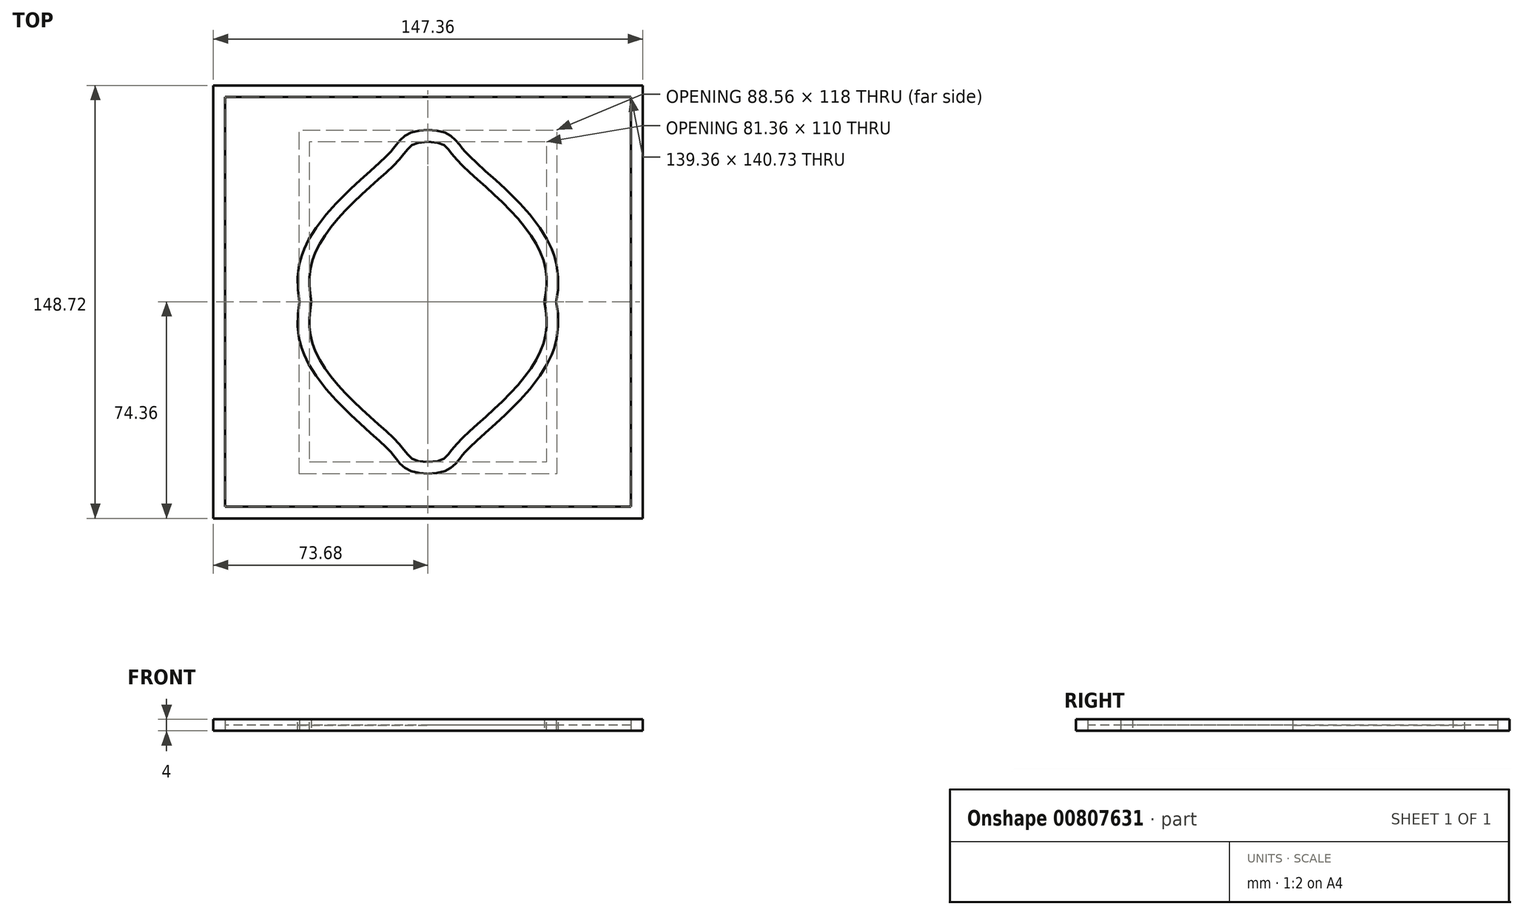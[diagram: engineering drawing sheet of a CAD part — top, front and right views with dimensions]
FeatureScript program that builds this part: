
annotation { "Feature Type Name" : "Feature", "Feature Type Description" : "" }
export const myFeature = defineFeature(function(context is Context, id is Id, definition is map)
    precondition{}
    {
        {
            var Q0;
            Q0=qCreatedBy(makeId("Top.planeOp"),FACE);
            var sketch = newSketch(context, id + "F0", { "sketchPlane" : qUnion([Q0])});
            skFitSpline(sketch, "E0", {"points": [v(-40, 0) * mm, v(-39.3, 15.26) * mm, v(-25.49, 34.27) * mm, v(-8.78, 50.1) * mm, v(0, 55) * mm], "startDerivative": vector(-12.5, 67.43) * mm, "endDerivative": vector(94.36, 0) * mm});
            skFitSpline(sketch, "E1.MirrorCS", {"points": [v(40, 0) * mm, v(39.3, 15.26) * mm, v(25.49, 34.27) * mm, v(8.78, 50.1) * mm, v(0, 55) * mm], "startDerivative": vector(12.5, 67.43) * mm, "endDerivative": vector(-94.36, 0) * mm});
            skFitSpline(sketch, "E2.MirrorCS", {"points": [v(-40, 0) * mm, v(-39.3, -15.26) * mm, v(-25.49, -34.27) * mm, v(-8.78, -50.1) * mm, v(0, -55) * mm], "startDerivative": vector(-12.5, -67.43) * mm, "endDerivative": vector(94.36, 0) * mm});
            skFitSpline(sketch, "E3.MirrorCS", {"points": [v(40, 0) * mm, v(39.3, -15.26) * mm, v(25.49, -34.27) * mm, v(8.78, -50.1) * mm, v(0, -55) * mm], "startDerivative": vector(12.5, -67.43) * mm, "endDerivative": vector(-94.36, 0) * mm});
            skFitSpline(sketch, "E4.0", {"points": [v(43.93, -0.73) * mm, v(44.07, 0.02) * mm, v(44.32, 1.53) * mm, v(44.59, 3.8) * mm, v(44.73, 6.09) * mm, v(44.7, 8.4) * mm, v(44.51, 10.74) * mm, v(44.18, 12.7) * mm, v(43.8, 14.28) * mm, v(43.52, 15.27) * mm, v(43.26, 16.07) * mm, v(43.06, 16.66) * mm, v(42.83, 17.25) * mm, v(42.52, 18.04) * mm, v(42.1, 19.02) * mm, v(41.35, 20.57) * mm, v(40.3, 22.49) * mm, v(38.89, 24.75) * mm, v(36.79, 27.73) * mm, v(34.43, 30.64) * mm, v(32.18, 33.13) * mm, v(30.86, 34.53) * mm, v(29.84, 35.58) * mm, v(28.81, 36.6) * mm, v(27.76, 37.63) * mm, v(26.7, 38.64) * mm, v(25.29, 39.97) * mm, v(23.52, 41.6) * mm, v(21.42, 43.47) * mm, v(19.4, 45.27) * mm, v(17.8, 46.7) * mm, v(16.6, 47.8) * mm, v(15.74, 48.6) * mm, v(14.94, 49.37) * mm, v(14.18, 50.11) * mm, v(13.6, 50.7) * mm, v(13.17, 51.16) * mm, v(12.86, 51.48) * mm, v(12.58, 51.8) * mm, v(12.35, 52.06) * mm, v(12.18, 52.26) * mm, v(12.06, 52.4) * mm, v(11.94, 52.54) * mm, v(11.83, 52.68) * mm, v(11.72, 52.82) * mm, v(11.57, 53.01) * mm, v(11.39, 53.26) * mm, v(11.16, 53.56) * mm, v(10.92, 53.88) * mm, v(10.67, 54.21) * mm, v(10.4, 54.56) * mm, v(10.1, 54.93) * mm, v(9.79, 55.3) * mm, v(9.43, 55.68) * mm, v(9.04, 56.07) * mm, v(8.6, 56.46) * mm, v(8.14, 56.83) * mm, v(7.62, 57.19) * mm, v(7.07, 57.52) * mm, v(6.48, 57.82) * mm, v(5.86, 58.09) * mm, v(5.22, 58.32) * mm, v(4.33, 58.57) * mm, v(3.16, 58.8) * mm, v(1.66, 58.97) * mm, v(0.57, 59) * mm, v(0, 59) * mm]});
            skFitSpline(sketch, "E4.1", {"points": [v(43.93, 0.73) * mm, v(44.07, -0.02) * mm, v(44.32, -1.53) * mm, v(44.59, -3.8) * mm, v(44.73, -6.09) * mm, v(44.7, -8.4) * mm, v(44.51, -10.74) * mm, v(44.18, -12.7) * mm, v(43.8, -14.28) * mm, v(43.52, -15.27) * mm, v(43.26, -16.07) * mm, v(43.06, -16.66) * mm, v(42.83, -17.25) * mm, v(42.52, -18.04) * mm, v(42.1, -19.02) * mm, v(41.35, -20.57) * mm, v(40.3, -22.49) * mm, v(38.89, -24.75) * mm, v(36.79, -27.73) * mm, v(34.43, -30.64) * mm, v(32.18, -33.13) * mm, v(30.86, -34.53) * mm, v(29.84, -35.58) * mm, v(28.81, -36.6) * mm, v(27.76, -37.63) * mm, v(26.7, -38.64) * mm, v(25.29, -39.97) * mm, v(23.52, -41.6) * mm, v(21.42, -43.47) * mm, v(19.4, -45.27) * mm, v(17.8, -46.7) * mm, v(16.6, -47.8) * mm, v(15.74, -48.6) * mm, v(14.94, -49.37) * mm, v(14.18, -50.11) * mm, v(13.6, -50.7) * mm, v(13.17, -51.16) * mm, v(12.86, -51.48) * mm, v(12.58, -51.8) * mm, v(12.35, -52.06) * mm, v(12.18, -52.26) * mm, v(12.06, -52.4) * mm, v(11.94, -52.54) * mm, v(11.83, -52.68) * mm, v(11.72, -52.82) * mm, v(11.57, -53.01) * mm, v(11.39, -53.26) * mm, v(11.16, -53.56) * mm, v(10.92, -53.88) * mm, v(10.67, -54.21) * mm, v(10.4, -54.56) * mm, v(10.1, -54.93) * mm, v(9.79, -55.3) * mm, v(9.43, -55.68) * mm, v(9.04, -56.07) * mm, v(8.6, -56.46) * mm, v(8.14, -56.83) * mm, v(7.62, -57.19) * mm, v(7.07, -57.52) * mm, v(6.48, -57.82) * mm, v(5.86, -58.09) * mm, v(5.22, -58.32) * mm, v(4.33, -58.57) * mm, v(3.16, -58.8) * mm, v(1.66, -58.97) * mm, v(0.57, -59) * mm, v(0, -59) * mm]});
            skFitSpline(sketch, "E4.2", {"points": [v(-43.93, 0.73) * mm, v(-44.07, -0.02) * mm, v(-44.32, -1.53) * mm, v(-44.59, -3.8) * mm, v(-44.73, -6.09) * mm, v(-44.7, -8.4) * mm, v(-44.51, -10.74) * mm, v(-44.18, -12.7) * mm, v(-43.8, -14.28) * mm, v(-43.52, -15.27) * mm, v(-43.26, -16.07) * mm, v(-43.06, -16.66) * mm, v(-42.83, -17.25) * mm, v(-42.52, -18.04) * mm, v(-42.1, -19.02) * mm, v(-41.35, -20.57) * mm, v(-40.3, -22.49) * mm, v(-38.89, -24.75) * mm, v(-36.79, -27.73) * mm, v(-34.43, -30.64) * mm, v(-32.18, -33.13) * mm, v(-30.86, -34.53) * mm, v(-29.84, -35.58) * mm, v(-28.81, -36.6) * mm, v(-27.76, -37.63) * mm, v(-26.7, -38.64) * mm, v(-25.29, -39.97) * mm, v(-23.52, -41.6) * mm, v(-21.42, -43.47) * mm, v(-19.4, -45.27) * mm, v(-17.8, -46.7) * mm, v(-16.6, -47.8) * mm, v(-15.74, -48.6) * mm, v(-14.94, -49.37) * mm, v(-14.18, -50.11) * mm, v(-13.6, -50.7) * mm, v(-13.17, -51.16) * mm, v(-12.86, -51.48) * mm, v(-12.58, -51.8) * mm, v(-12.35, -52.06) * mm, v(-12.18, -52.26) * mm, v(-12.06, -52.4) * mm, v(-11.94, -52.54) * mm, v(-11.83, -52.68) * mm, v(-11.72, -52.82) * mm, v(-11.57, -53.01) * mm, v(-11.39, -53.26) * mm, v(-11.16, -53.56) * mm, v(-10.92, -53.88) * mm, v(-10.67, -54.21) * mm, v(-10.4, -54.56) * mm, v(-10.1, -54.93) * mm, v(-9.79, -55.3) * mm, v(-9.43, -55.68) * mm, v(-9.04, -56.07) * mm, v(-8.6, -56.46) * mm, v(-8.14, -56.83) * mm, v(-7.62, -57.19) * mm, v(-7.07, -57.52) * mm, v(-6.48, -57.82) * mm, v(-5.86, -58.09) * mm, v(-5.22, -58.32) * mm, v(-4.33, -58.57) * mm, v(-3.16, -58.8) * mm, v(-1.66, -58.97) * mm, v(-0.57, -59) * mm, v(0, -59) * mm]});
            skFitSpline(sketch, "E4.3", {"points": [v(-43.93, -0.73) * mm, v(-44.07, 0.02) * mm, v(-44.32, 1.53) * mm, v(-44.59, 3.8) * mm, v(-44.73, 6.09) * mm, v(-44.7, 8.4) * mm, v(-44.51, 10.74) * mm, v(-44.18, 12.7) * mm, v(-43.8, 14.28) * mm, v(-43.52, 15.27) * mm, v(-43.26, 16.07) * mm, v(-43.06, 16.66) * mm, v(-42.83, 17.25) * mm, v(-42.52, 18.04) * mm, v(-42.1, 19.02) * mm, v(-41.35, 20.57) * mm, v(-40.3, 22.49) * mm, v(-38.89, 24.75) * mm, v(-36.79, 27.73) * mm, v(-34.43, 30.64) * mm, v(-32.18, 33.13) * mm, v(-30.86, 34.53) * mm, v(-29.84, 35.58) * mm, v(-28.81, 36.6) * mm, v(-27.76, 37.63) * mm, v(-26.7, 38.64) * mm, v(-25.29, 39.97) * mm, v(-23.52, 41.6) * mm, v(-21.42, 43.47) * mm, v(-19.4, 45.27) * mm, v(-17.8, 46.7) * mm, v(-16.6, 47.8) * mm, v(-15.74, 48.6) * mm, v(-14.94, 49.37) * mm, v(-14.18, 50.11) * mm, v(-13.6, 50.7) * mm, v(-13.17, 51.16) * mm, v(-12.86, 51.48) * mm, v(-12.58, 51.8) * mm, v(-12.35, 52.06) * mm, v(-12.18, 52.26) * mm, v(-12.06, 52.4) * mm, v(-11.94, 52.54) * mm, v(-11.83, 52.68) * mm, v(-11.72, 52.82) * mm, v(-11.57, 53.01) * mm, v(-11.39, 53.26) * mm, v(-11.16, 53.56) * mm, v(-10.92, 53.88) * mm, v(-10.67, 54.21) * mm, v(-10.4, 54.56) * mm, v(-10.1, 54.93) * mm, v(-9.79, 55.3) * mm, v(-9.43, 55.68) * mm, v(-9.04, 56.07) * mm, v(-8.6, 56.46) * mm, v(-8.14, 56.83) * mm, v(-7.62, 57.19) * mm, v(-7.07, 57.52) * mm, v(-6.48, 57.82) * mm, v(-5.86, 58.09) * mm, v(-5.22, 58.32) * mm, v(-4.33, 58.57) * mm, v(-3.16, 58.8) * mm, v(-1.66, 58.97) * mm, v(-0.57, 59) * mm, v(0, 59) * mm]});
            skLineSegment(sketch, "E5.bottom", {"start": v(73.68, 74.36) * mm, "end": v(-73.68, 74.36) * mm});
            skLineSegment(sketch, "E5.top", {"start": v(73.68, -74.36) * mm, "end": v(-73.68, -74.36) * mm});
            skLineSegment(sketch, "E5.left", {"start": v(73.68, 74.36) * mm, "end": v(73.68, -74.36) * mm});
            skLineSegment(sketch, "E5.right", {"start": v(-73.68, 74.36) * mm, "end": v(-73.68, -74.36) * mm});
            skPoint(sketch, "E5.middle", {"position": v(0, 0) * mm});
            skLineSegment(sketch, "E6.0", {"start": v(69.68, 70.36) * mm, "end": v(-69.68, 70.36) * mm});
            skLineSegment(sketch, "E6.1", {"start": v(69.68, 70.36) * mm, "end": v(69.68, -70.36) * mm});
            skLineSegment(sketch, "E6.2", {"start": v(69.68, -70.36) * mm, "end": v(-69.68, -70.36) * mm});
            skLineSegment(sketch, "E6.3", {"start": v(-69.68, 70.36) * mm, "end": v(-69.68, -70.36) * mm});
            skSolve(sketch);
        }
        {
            var Q0;
            Q0=makeQuery(id+"F0.imprint","IMPRINT",FACE,{"disambiguationData":[TD([[makeQuery(id+"F0.imprint","IMPRINT",EDGE,{"derivedFrom":sQuery(id+"F0.wireOp",EDGE,"E0")}),1.0]])]});
            var Q1;
            Q1=makeQuery(id+"F0.imprint","IMPRINT",FACE,{"disambiguationData":[TD([[makeQuery(id+"F0.imprint","IMPRINT",EDGE,{"derivedFrom":sQuery(id+"F0.wireOp",EDGE,"E5.bottom")}),1.0]])]});
            extrude(context, id + "F1", {"entities" : qUnion([Q0, Q1]), "depth" : 4 * mm, "offsetDistance" : 25 * mm});
        }
        {
            var Q0;
            Q0=makeQuery(id+"F0.imprint","IMPRINT",FACE,{"disambiguationData":[TD([[makeQuery(id+"F0.imprint","IMPRINT",EDGE,{"derivedFrom":sQuery(id+"F0.wireOp",EDGE,"E4.0")}),-1.0]])]});
            extrude(context, id + "F2", {"entities" : qUnion([Q0]), "depth" : 2 * mm, "offsetDistance" : 25 * mm});
        }
    });
